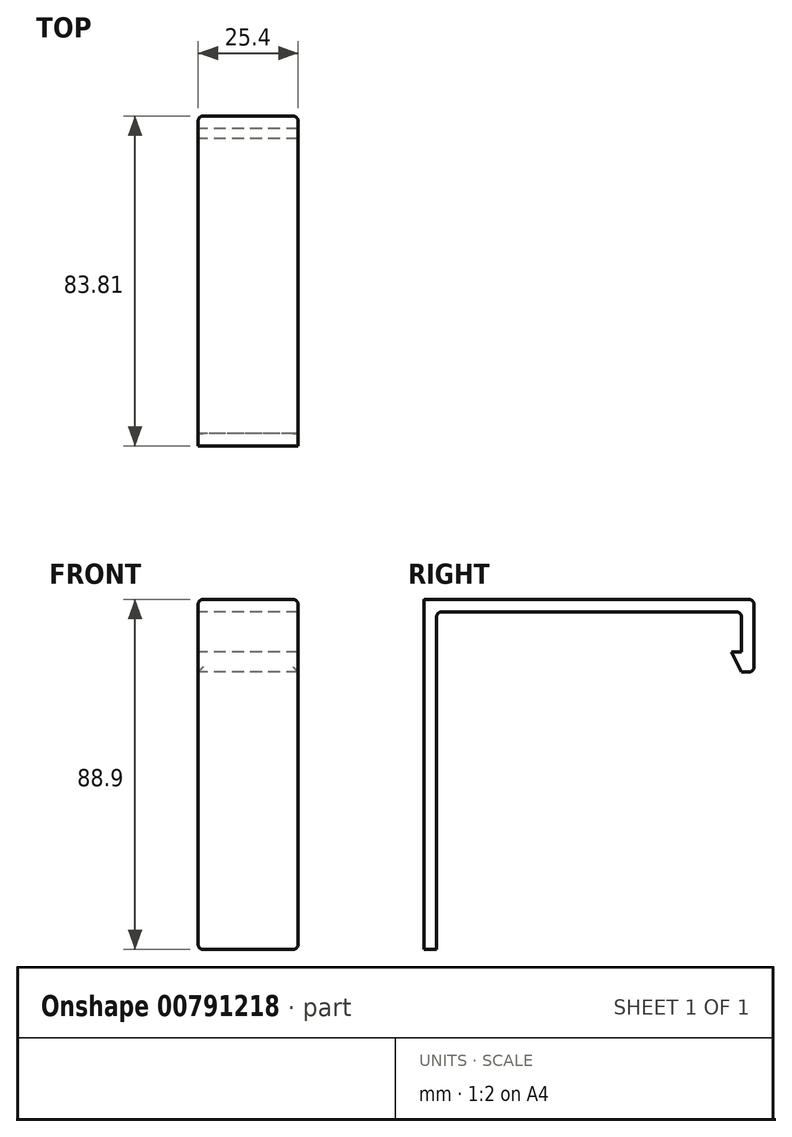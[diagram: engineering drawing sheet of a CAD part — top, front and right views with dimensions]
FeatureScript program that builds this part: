
annotation { "Feature Type Name" : "Feature", "Feature Type Description" : "" }
export const myFeature = defineFeature(function(context is Context, id is Id, definition is map)
    precondition{}
    {
        {
            var Q0;
            Q0=qCreatedBy(makeId("Right.planeOp"),FACE);
            var sketch = newSketch(context, id + "F0", { "sketchPlane" : qUnion([Q0])});
            skLineSegment(sketch, "E0", {"start": v(0, 49.79) * mm, "end": v(77.47, 49.79) * mm});
            skLineSegment(sketch, "E1", {"start": v(77.47, 49.79) * mm, "end": v(77.47, 39.63) * mm});
            skLineSegment(sketch, "E2", {"start": v(77.47, 39.63) * mm, "end": v(77.47, 34.55) * mm});
            skLineSegment(sketch, "E3", {"start": v(77.47, 34.55) * mm, "end": v(80.64, 34.55) * mm});
            skLineSegment(sketch, "E4", {"start": v(80.64, 34.55) * mm, "end": v(80.64, 49.79) * mm});
            skLineSegment(sketch, "E5", {"start": v(80.64, 49.79) * mm, "end": v(80.64, 52.96) * mm});
            skLineSegment(sketch, "E6", {"start": v(80.64, 52.96) * mm, "end": v(77.47, 52.96) * mm});
            skLineSegment(sketch, "E7", {"start": v(77.47, 52.96) * mm, "end": v(0, 52.96) * mm});
            skLineSegment(sketch, "E8", {"start": v(0, 52.96) * mm, "end": v(-3.17, 52.96) * mm});
            skLineSegment(sketch, "E9", {"start": v(-3.18, 52.96) * mm, "end": v(-3.18, 49.79) * mm});
            skLineSegment(sketch, "E10", {"start": v(-3.18, 49.79) * mm, "end": v(-3.18, 11.69) * mm});
            skLineSegment(sketch, "E11", {"start": v(-3.18, 11.69) * mm, "end": v(-3.18, -35.94) * mm});
            skLineSegment(sketch, "E12", {"start": v(-3.17, -35.94) * mm, "end": v(0, -35.94) * mm});
            skLineSegment(sketch, "E13", {"start": v(0, -35.94) * mm, "end": v(0, 49.79) * mm});
            skLineSegment(sketch, "E14", {"start": v(77.47, 39.63) * mm, "end": v(74.93, 39.63) * mm});
            skLineSegment(sketch, "E15", {"start": v(74.93, 39.63) * mm, "end": v(77.47, 34.55) * mm});
            skSolve(sketch);
        }
        {
            var Q0;
            Q0=makeQuery(id+"F0.imprint","IMPRINT",FACE,{"disambiguationData":[TD([[makeQuery(id+"F0.imprint","IMPRINT",EDGE,{"derivedFrom":sQuery(id+"F0.wireOp",EDGE,"E0")}),1.0]])]});
            var Q1;
            Q1=makeQuery(id+"F0.imprint","IMPRINT",FACE,{"disambiguationData":[TD([[makeQuery(id+"F0.imprint","IMPRINT",EDGE,{"derivedFrom":sQuery(id+"F0.wireOp",EDGE,"E2")}),-1.0]])]});
            extrude(context, id + "F1", {"entities" : qUnion([Q0, Q1]), "depth" : 25.4 * mm, "offsetDistance" : 25.4 * mm});
        }
        {
            var Q0;
            Q0=makeQuery(id+"F1.opExtrude","CAP_EDGE",EDGE,{"disambiguationData":[OSD([sQuery(id+"F0.wireOp",EDGE,"E6"),sQuery(id+"F0.wireOp",EDGE,"E7"),sQuery(id+"F0.wireOp",EDGE,"E8")])],"isStart":false});
            var Q1;
            Q1=makeQuery(id+"F1.opExtrude","CAP_EDGE",EDGE,{"disambiguationData":[OSD([sQuery(id+"F0.wireOp",EDGE,"E6"),sQuery(id+"F0.wireOp",EDGE,"E7"),sQuery(id+"F0.wireOp",EDGE,"E8")])],"isStart":true});
            var Q2;
            Q2=makeQuery(id+"F1.opExtrude","SWEPT_EDGE",EDGE,{"disambiguationData":[OSD([sQuery(id+"F0.wireOp",EDGE,"E5"),sQuery(id+"F0.wireOp",EDGE,"E6")])]});
            var Q3;
            Q3=makeQuery(id+"F1.opExtrude","CAP_EDGE",EDGE,{"disambiguationData":[OSD([sQuery(id+"F0.wireOp",EDGE,"E4"),sQuery(id+"F0.wireOp",EDGE,"E5")])],"isStart":false});
            var Q4;
            Q4=makeQuery(id+"F1.opExtrude","SWEPT_EDGE",EDGE,{"disambiguationData":[OSD([sQuery(id+"F0.wireOp",EDGE,"E3"),sQuery(id+"F0.wireOp",EDGE,"E4")])]});
            var Q5;
            Q5=makeQuery(id+"F1.opExtrude","CAP_EDGE",EDGE,{"disambiguationData":[OSD([sQuery(id+"F0.wireOp",EDGE,"E4"),sQuery(id+"F0.wireOp",EDGE,"E5")])],"isStart":true});
            var Q6;
            Q6=makeQuery(id+"F1.opExtrude","CAP_EDGE",EDGE,{"disambiguationData":[OSD([sQuery(id+"F0.wireOp",EDGE,"E12")])],"isStart":false});
            var Q7;
            Q7=makeQuery(id+"F1.opExtrude","CAP_EDGE",EDGE,{"disambiguationData":[OSD([sQuery(id+"F0.wireOp",EDGE,"E12")])],"isStart":true});
            fillet(context, id + "F2", {"entities" : qUnion([Q0, Q1, Q2, Q3, Q4, Q5, Q6, Q7]), "radius" : 1.27 * mm, "tangentPropagation" : true, "allowEdgeOverflow" : false});
        }
        {
            var Q0;
            Q0=makeQuery(id+"F1.opExtrude","SWEPT_EDGE",EDGE,{"disambiguationData":[OSD([sQuery(id+"F0.wireOp",EDGE,"E0"),sQuery(id+"F0.wireOp",EDGE,"E13")])]});
            var Q1;
            Q1=makeQuery(id+"F1.opExtrude","SWEPT_EDGE",EDGE,{"disambiguationData":[OSD([sQuery(id+"F0.wireOp",EDGE,"E0"),sQuery(id+"F0.wireOp",EDGE,"E1")])]});
            fillet(context, id + "F3", {"entities" : qUnion([Q0, Q1]), "radius" : 1.27 * mm, "tangentPropagation" : true, "allowEdgeOverflow" : false});
        }
    });
